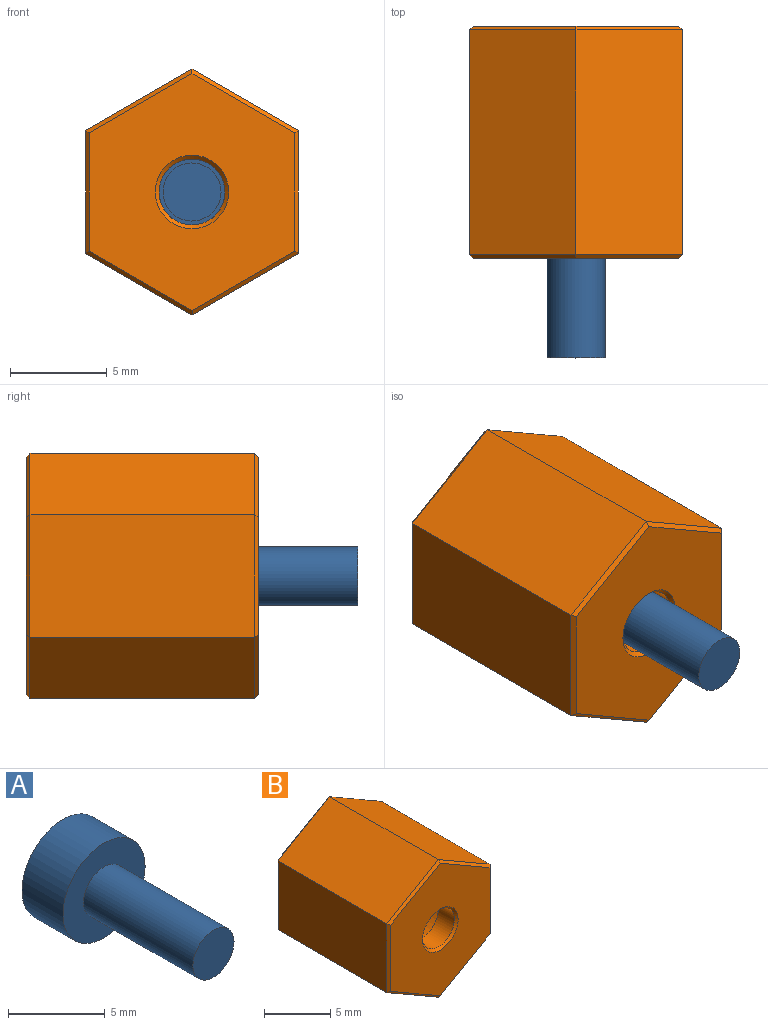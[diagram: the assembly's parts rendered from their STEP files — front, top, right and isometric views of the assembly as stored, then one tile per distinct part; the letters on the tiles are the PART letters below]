
ASSEMBLY  parts=2 mates=1
PART A: 5 faces, bbox 6x11x6 mm
  f0: cylinder r=3mm len=6mm, axis (0,1,0), area 56.5mm2, adj f1,f2
  f1: plane 6x6mm, normal (0,-1,0), area 21.2mm2, adj f0,f3
  f2: plane 6x6mm, normal (0,1,0), area 28.3mm2, adj f0
  f3: cylinder r=1.5mm len=8mm, axis (0,1,0), area 75.4mm2, adj f1,f4
  f4: plane 3x3mm, normal (0,-1,0), area 7.1mm2, adj f3
PART B: 25 faces, bbox 11x12x12.7 mm
  f0: cone r=0mm half-angle=59deg, axis (0,1,0), area 34.3mm2, adj f9,f10
  f1: plane 11.6x6.35mm, normal (1,0,0), area 73.7mm2, adj f2,f6,f16,f20
  f2: plane 11.6x5.5mm, normal (0.5,0,0.87), area 73.7mm2, adj f1,f3,f17,f19
  f3: plane 11.6x5.5mm, normal (-0.5,0,0.87), area 73.7mm2, adj f2,f4,f15,f21
  f4: plane 11.6x6.35mm, normal (-1,0,0), area 73.7mm2, adj f3,f5,f13,f23
  f5: plane 11.6x5.5mm, normal (-0.5,0,-0.87), area 73.7mm2, adj f4,f6,f12,f24
  f6: plane 11.6x5.5mm, normal (0.5,0,-0.87), area 73.7mm2, adj f1,f5,f14,f22
  f7: plane 12.24x10.6mm, normal (0,-1,0), area 86mm2, adj f18,f19,f20,f21,f22,f23,f24
  f8: plane 12.24x10.6mm, normal (0,1,0), area 54.3mm2, adj f11,f12,f13,f14,f15,f16,f17
  f9: cylinder r=3.5mm len=8.8mm, axis (0,1,0), area 193.5mm2, adj f0,f11
  f10: cylinder r=1.7mm len=3.4mm, axis (0,-1,0), area 18.4mm2, adj f0,f18
  f11: cone r=3.5mm half-angle=45deg, axis (0,1,0), area 6.4mm2, adj f8,f9
  f12: plane 5.5x3.29mm, normal (-0.35,0.71,-0.61), area 1.8mm2, adj f5,f8,f13,f14
  f13: plane 6.35x0.2mm, normal (-0.71,0.71,0), area 1.8mm2, adj f4,f8,f12,f15
  f14: plane 5.5x3.29mm, normal (0.35,0.71,-0.61), area 1.8mm2, adj f6,f8,f12,f16
  f15: plane 5.5x3.29mm, normal (-0.35,0.71,0.61), area 1.8mm2, adj f3,f8,f13,f17
  f16: plane 6.35x0.2mm, normal (0.71,0.71,0), area 1.8mm2, adj f1,f8,f14,f17
  f17: plane 5.5x3.29mm, normal (0.35,0.71,0.61), area 1.8mm2, adj f2,f8,f15,f16
  f18: cone r=1.7mm half-angle=45deg, axis (0,-1,0), area 3.2mm2, adj f7,f10
  f19: plane 5.5x3.29mm, normal (0.35,-0.71,0.61), area 1.8mm2, adj f2,f7,f20,f21
  f20: plane 6.35x0.2mm, normal (0.71,-0.71,0), area 1.8mm2, adj f1,f7,f19,f22
  f21: plane 5.5x3.29mm, normal (-0.35,-0.71,0.61), area 1.8mm2, adj f3,f7,f19,f23
  f22: plane 5.5x3.29mm, normal (0.35,-0.71,-0.61), area 1.8mm2, adj f6,f7,f20,f24
  f23: plane 6.35x0.2mm, normal (-0.71,-0.71,0), area 1.8mm2, adj f4,f7,f21,f24
  f24: plane 5.5x3.29mm, normal (-0.35,-0.71,-0.61), area 1.8mm2, adj f5,f7,f22,f23
PLACE A t=(-7.27,-2.62,-0.43)mm
PLACE B t=(-7.27,3.52,-0.43)mm
MATE fastened A.f0 <-> B.f0  axis (0,1,0) through (-7.27,-5.62,-0.43)mm
